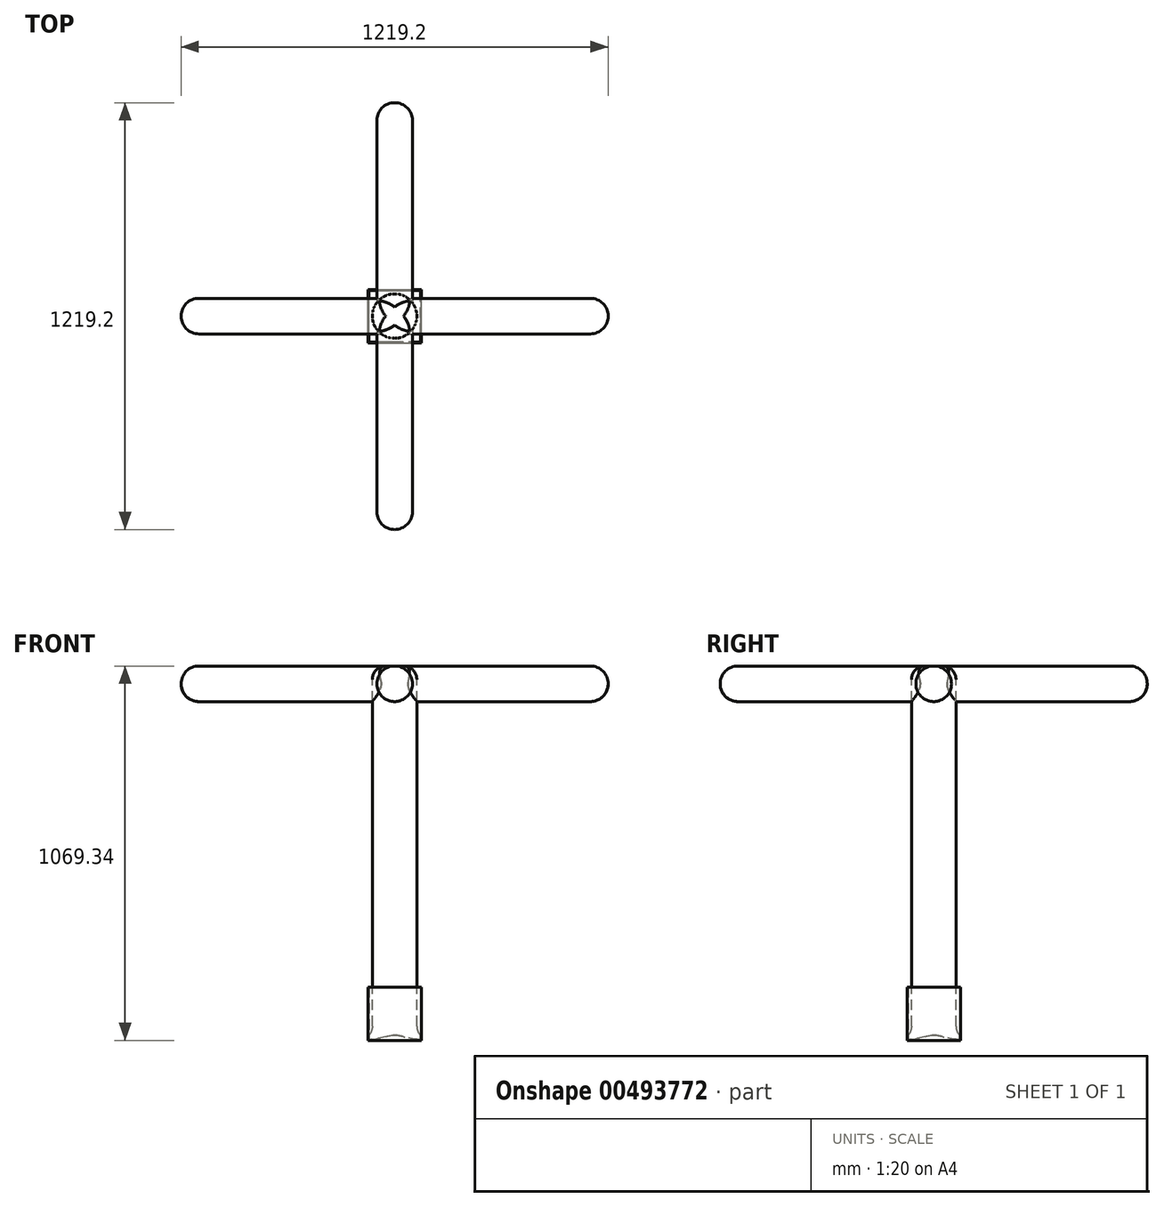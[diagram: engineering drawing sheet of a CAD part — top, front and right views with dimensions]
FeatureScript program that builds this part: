
annotation { "Feature Type Name" : "Feature", "Feature Type Description" : "" }
export const myFeature = defineFeature(function(context is Context, id is Id, definition is map)
    precondition{}
    {
        {
            var Q0;
            Q0=qCreatedBy(makeId("Top.planeOp"),FACE);
            var sketch = newSketch(context, id + "F0", { "sketchPlane" : qUnion([Q0])});
            skLineSegment(sketch, "E0.bottom", {"start": v(76.2, 76.2) * mm, "end": v(-76.2, 76.2) * mm});
            skLineSegment(sketch, "E0.top", {"start": v(76.2, -76.2) * mm, "end": v(-76.2, -76.2) * mm});
            skLineSegment(sketch, "E0.left", {"start": v(76.2, 76.2) * mm, "end": v(76.2, -76.2) * mm});
            skLineSegment(sketch, "E0.right", {"start": v(-76.2, 76.2) * mm, "end": v(-76.2, -76.2) * mm});
            skPoint(sketch, "E0.middle", {"position": v(0, 0) * mm});
            skSolve(sketch);
        }
        {
            var Q0;
            Q0=makeQuery(id+"F0.imprint","IMPRINT",FACE,{"disambiguationData":[TD([[makeQuery(id+"F0.imprint","IMPRINT",EDGE,{"derivedFrom":sQuery(id+"F0.wireOp",EDGE,"E0.bottom")}),1.0]])]});
            extrude(context, id + "F1", {"entities" : qUnion([Q0]), "depth" : 152.4 * mm, "offsetDistance" : 25.4 * mm});
        }
        {
            var Q0;
            Q0=makeQuery(id+"F1.opExtrude","CAP_FACE",FACE,{"disambiguationData":[OSD([sQuery(id+"F0.wireOp",EDGE,"E0.bottom"),sQuery(id+"F0.wireOp",EDGE,"E0.top"),sQuery(id+"F0.wireOp",EDGE,"E0.left"),sQuery(id+"F0.wireOp",EDGE,"E0.right")])],"isStart":false});
            shell(context, id + "F2", {"entities" : qUnion([Q0]), "thickness" : 2.54 * mm});
        }
        {
            var Q0;
            Q0=makeQuery(id+"F2.opShell","OFFSET_FACE",FACE,{"disambiguationData":[OSD([sQuery(id+"F0.wireOp",EDGE,"E0.bottom"),sQuery(id+"F0.wireOp",EDGE,"E0.top"),sQuery(id+"F0.wireOp",EDGE,"E0.left"),sQuery(id+"F0.wireOp",EDGE,"E0.right")])]});
            var sketch = newSketch(context, id + "F3", { "sketchPlane" : qUnion([Q0])});
            skCircle(sketch, "E1", {"center": v(0, 0) * mm, "radius": 63.5 * mm});
            skSolve(sketch);
        }
        {
            var Q0;
            Q0=qCreatedBy(makeId("Front.planeOp"),FACE);
            var sketch = newSketch(context, id + "F4", { "sketchPlane" : qUnion([Q0])});
            skLineSegment(sketch, "E2", {"start": v(0, 0) * mm, "end": v(0, 1066.8) * mm});
            skSolve(sketch);
        }
        {
            var Q0;
            Q0=makeQuery(id+"F3.imprint","IMPRINT",FACE,{"disambiguationData":[TD([[makeQuery(id+"F3.imprint","IMPRINT",EDGE,{"derivedFrom":sQuery(id+"F3.wireOp",EDGE,"E1")}),-1.0]])]});
            cPlane(context, id + "F5", {"entities" : qUnion([Q0]), "cplaneType" : CPlaneType.OFFSET, "offset" : 1066.8 * mm, "width" : 152.4 * mm, "height" : 152.4 * mm});
        }
        {
            var Q0;
            Q0=qCreatedBy(id+"F5.planeOp",FACE);
            var sketch = newSketch(context, id + "F6", { "sketchPlane" : qUnion([Q0])});
            skCircle(sketch, "E3", {"center": v(0, 0) * mm, "radius": 63.5 * mm});
            skSolve(sketch);
        }
        {
            var Q1;
            Q1=makeQuery(id+"F3.imprint","IMPRINT",FACE,{"disambiguationData":[TD([[makeQuery(id+"F3.imprint","IMPRINT",EDGE,{"derivedFrom":sQuery(id+"F3.wireOp",EDGE,"E1")}),1.0]])]});
            var Q2;
            Q2=makeQuery(id+"F6.imprint","IMPRINT",FACE,{"disambiguationData":[TD([[makeQuery(id+"F6.imprint","IMPRINT",EDGE,{"derivedFrom":sQuery(id+"F6.wireOp",EDGE,"E3")}),1.0]])]});
            loft(context, id + "F7", {"operationType" : NewBodyOperationType.ADD, "sheetProfilesArray" : [{ "sheetProfileEntities" : qUnion([Q1]) }, { "sheetProfileEntities" : qUnion([Q2]) }]});
        }
        {
            var Q0;
            Q0=makeQuery(id+"F7.opLoft","SWEPT_FACE",FACE,{"disambiguationData":[OSD([sQuery(id+"F3.wireOp",EDGE,"E1"),sQuery(id+"F6.wireOp",EDGE,"E3")])]});
            fillet(context, id + "F8", {"entities" : qUnion([Q0]), "radius" : 38.1 * mm, "tangentPropagation" : true, "allowEdgeOverflow" : false});
        }
        {
            var Q0;
            Q0=qCreatedBy(makeId("Right.planeOp"),FACE);
            var sketch = newSketch(context, id + "F9", { "sketchPlane" : qUnion([Q0])});
            skCircle(sketch, "E4", {"center": v(0, 1018.54) * mm, "radius": 50.8 * mm});
            skSolve(sketch);
        }
        {
            var Q0;
            Q0 = qSketchRegion(id + "F9", true);
            extrude(context, id + "F10", {"entities" : qUnion([Q0]), "operationType" : NewBodyOperationType.ADD, "depth" : 1219.2 * mm, "offsetDistance" : 25.4 * mm, "symmetric" : true});
        }
        {
            var Q0;
            Q0=makeQuery(id+"F10.opExtrude","CAP_EDGE",EDGE,{"disambiguationData":[OSD([sQuery(id+"F9.wireOp",EDGE,"E4")])],"isStart":true});
            var Q1;
            Q1=makeQuery(id+"F10.opExtrude","CAP_EDGE",EDGE,{"disambiguationData":[OSD([sQuery(id+"F9.wireOp",EDGE,"E4")])],"isStart":false});
            fillet(context, id + "F11", {"entities" : qUnion([Q0, Q1]), "radius" : 50.8 * mm, "tangentPropagation" : true, "allowEdgeOverflow" : false});
        }
        {
            var Q0;
            Q0=makeQuery(id+"F1.opExtrude","SWEPT_BODY",BODY,{"disambiguationData":[OSD([sQuery(id+"F0.wireOp",EDGE,"E0.bottom"),sQuery(id+"F0.wireOp",EDGE,"E0.top"),sQuery(id+"F0.wireOp",EDGE,"E0.left"),sQuery(id+"F0.wireOp",EDGE,"E0.right")])]});
            var Q1;
            Q1=sQuery(id+"F4.wireOp",EDGE,"E2");
            circularPattern(context, id + "F12", {"entities" : qUnion([Q0]), "axis" : qUnion([Q1]), "angle" : 360 * degree, "instanceCount" : 4, "equalSpace" : true});
        }
    });
